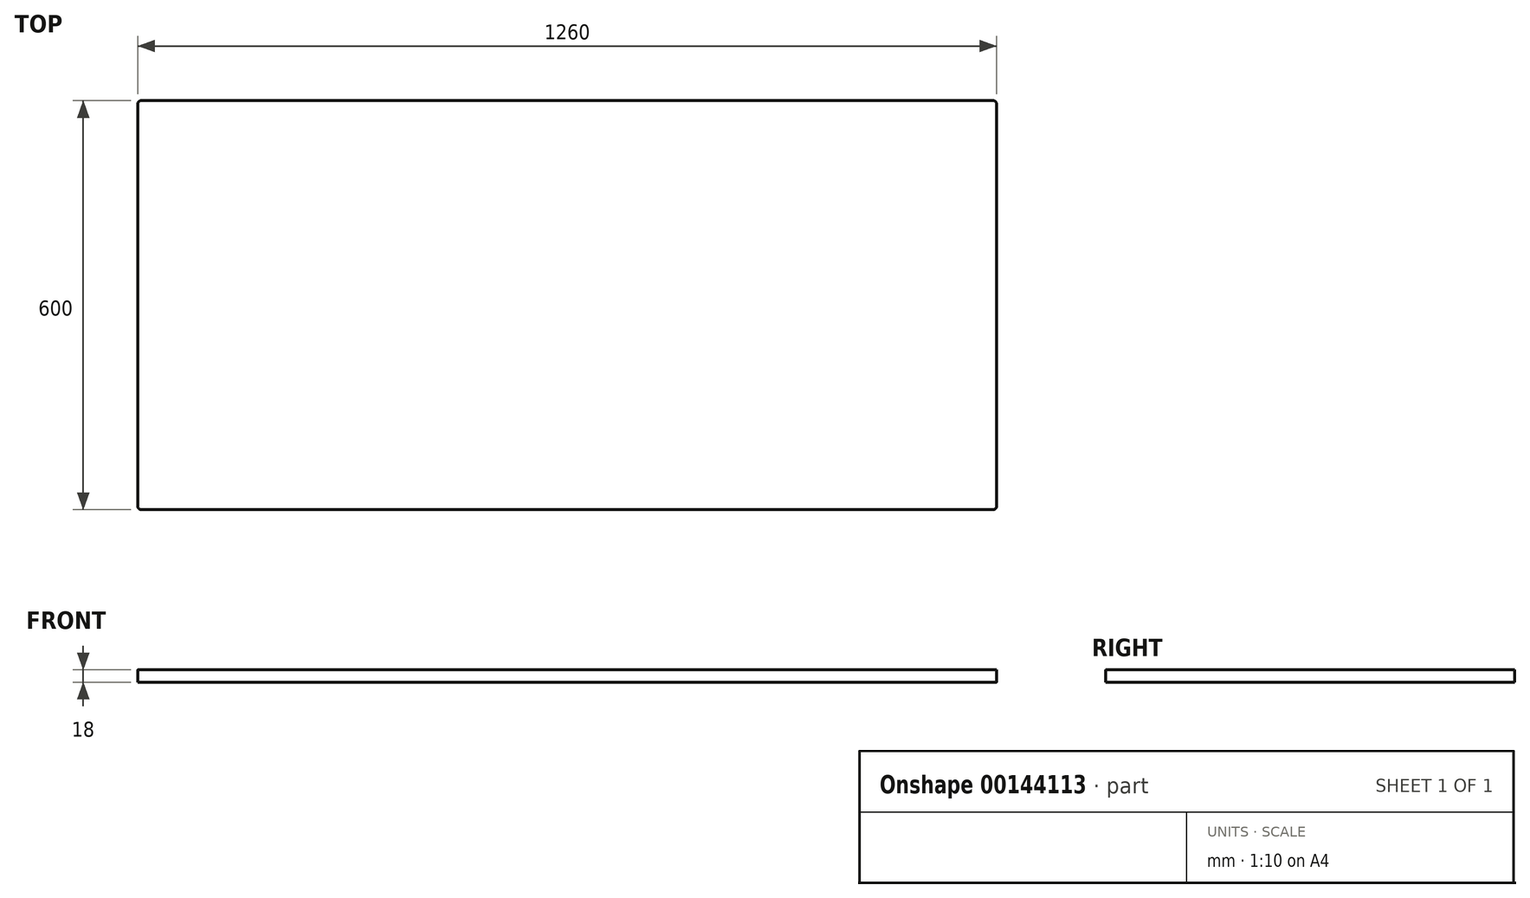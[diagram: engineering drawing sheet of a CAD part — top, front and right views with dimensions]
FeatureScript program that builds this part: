
annotation { "Feature Type Name" : "Feature", "Feature Type Description" : "" }
export const myFeature = defineFeature(function(context is Context, id is Id, definition is map)
    precondition{}
    {
        {
            var Q0;
            Q0=qCreatedBy(makeId("Top.planeOp"),FACE);
            var sketch = newSketch(context, id + "F0", { "sketchPlane" : qUnion([Q0])});
            skLineSegment(sketch, "E0.bottom", {"start": v(625, 300) * mm, "end": v(-625, 300) * mm});
            skLineSegment(sketch, "E0.top", {"start": v(625, -300) * mm, "end": v(-625, -300) * mm});
            skLineSegment(sketch, "E0.left", {"start": v(630, 295) * mm, "end": v(630, -295) * mm});
            skLineSegment(sketch, "E0.right", {"start": v(-630, 295) * mm, "end": v(-630, -295) * mm});
            skPoint(sketch, "E0.middle", {"position": v(0, 0) * mm});
            skPoint(sketch, "E1.visualSharp", {"position": v(-630, 300) * mm});
            skArc(sketch, "E1.filletArc", {"start": v(-625, 300) * mm, "mid": v(-628.54, 298.54) * mm, "end": v(-630, 295) * mm});
            skPoint(sketch, "E2.visualSharp", {"position": v(-630, -300) * mm});
            skArc(sketch, "E2.filletArc", {"start": v(-630, -295) * mm, "mid": v(-628.54, -298.54) * mm, "end": v(-625, -300) * mm});
            skPoint(sketch, "E3.visualSharp", {"position": v(630, 300) * mm});
            skArc(sketch, "E3.filletArc", {"start": v(630, 295) * mm, "mid": v(628.54, 298.54) * mm, "end": v(625, 300) * mm});
            skPoint(sketch, "E4.visualSharp", {"position": v(630, -300) * mm});
            skArc(sketch, "E4.filletArc", {"start": v(625, -300) * mm, "mid": v(628.54, -298.54) * mm, "end": v(630, -295) * mm});
            skSolve(sketch);
        }
        {
            var Q0;
            Q0=makeQuery(id+"F0.imprint","IMPRINT",FACE,{"disambiguationData":[TD([[makeQuery(id+"F0.imprint","IMPRINT",EDGE,{"derivedFrom":sQuery(id+"F0.wireOp",EDGE,"E0.bottom")}),1.0]])]});
            extrude(context, id + "F1", {"entities" : qUnion([Q0]), "depth" : 18 * mm});
        }
    });
